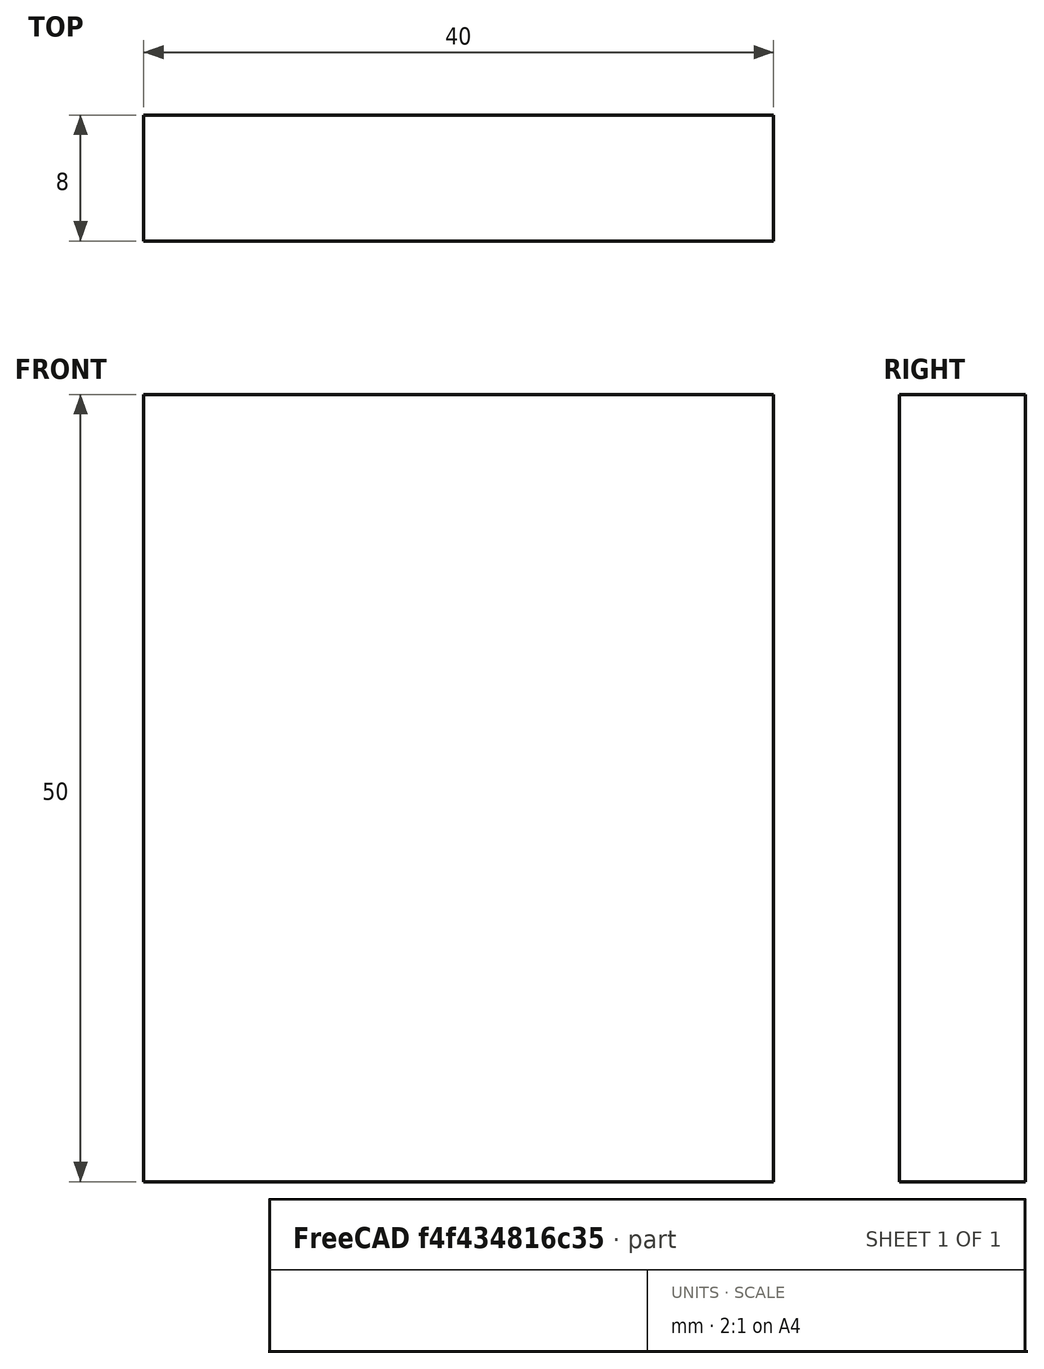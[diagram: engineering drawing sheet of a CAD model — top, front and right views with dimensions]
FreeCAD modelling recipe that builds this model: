
FCSTD DOCUMENT  (FreeCAD 0.15R4671 (Git))
Label: Flat Bar 40x8 EN10058 S235JR
License: All rights reserved
LicenseURL: http://en.wikipedia.org/wiki/All_rights_reserved
objects: Sketcher::SketchObject×1, Part::Extrusion×1
note: 2 computed .brp shape members not serialized (recipe doc carries the construction recipe); baked Part::Feature solids carry a one-line shape summary decoded from their .brp

FEATURE [Sketcher::SketchObject] Sketch
  sketch-geometry (4):
    g0: LineSegment StartX=-20 StartY=-4 StartZ=0 EndX=20 EndY=-4 EndZ=0
    g1: LineSegment StartX=20 StartY=-4 StartZ=0 EndX=20 EndY=4 EndZ=0
    g2: LineSegment StartX=20 StartY=4 StartZ=0 EndX=-20 EndY=4 EndZ=0
    g3: LineSegment StartX=-20 StartY=4 StartZ=0 EndX=-20 EndY=-4 EndZ=0
  constraints (12):
    c: Coincident(g0,g1)
    c: Coincident(g1,g2)
    c: Coincident(g2,g3)
    c: Coincident(g3,g0)
    c: Horizontal(g0)
    c: Horizontal(g2)
    c: Vertical(g1)
    c: Vertical(g3)
    c: Symmetric(g1,g2,g-2)
    c: Symmetric(g0,g1,g-1)
    c: DistanceY(g1) = 8
    c: DistanceX(g0) = 40
FEATURE [Part::Extrusion] Extrude  label="Flat Bar 40x8 EN10058 S235JR"
  Base = -> Sketch
  Dir = (0,0,50)
  Solid = true
